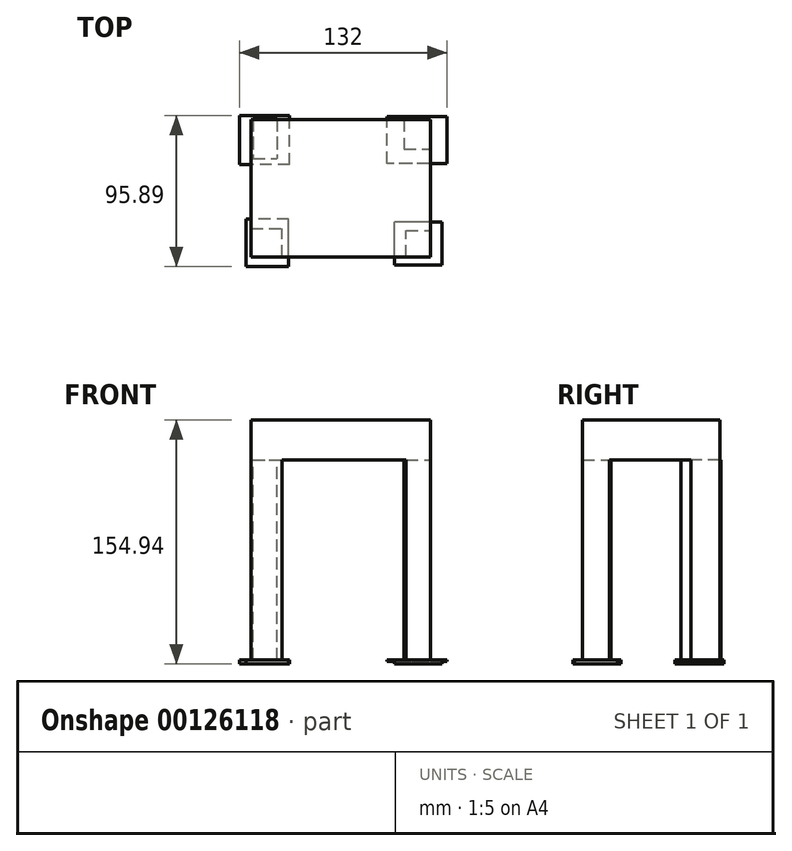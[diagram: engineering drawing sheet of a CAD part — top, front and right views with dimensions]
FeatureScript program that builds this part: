
annotation { "Feature Type Name" : "Feature", "Feature Type Description" : "" }
export const myFeature = defineFeature(function(context is Context, id is Id, definition is map)
    precondition{}
    {
        {
            var Q0;
            Q0=qCreatedBy(makeId("Top.planeOp"),FACE);
            var sketch = newSketch(context, id + "F0", { "sketchPlane" : qUnion([Q0])});
            skLineSegment(sketch, "E0.bottom", {"start": v(-57.47, 12.99) * mm, "end": v(56.4, 12.99) * mm});
            skLineSegment(sketch, "E0.top", {"start": v(-57.47, -23.38) * mm, "end": v(56.4, -23.38) * mm});
            skLineSegment(sketch, "E0.left", {"start": v(-57.47, 12.99) * mm, "end": v(-57.47, -23.38) * mm});
            skLineSegment(sketch, "E0.right", {"start": v(56.4, 12.99) * mm, "end": v(56.4, -23.38) * mm});
            skSolve(sketch);
        }
        {
            var Q0;
            Q0=makeQuery(id+"F0.imprint","IMPRINT",FACE,{"disambiguationData":[TD([[makeQuery(id+"F0.imprint","IMPRINT",EDGE,{"derivedFrom":sQuery(id+"F0.wireOp",EDGE,"E0.bottom")}),-1.0]])]});
            extrude(context, id + "F1", {"entities" : qUnion([Q0]), "depth" : 25.4 * mm});
        }
        {
            var Q0;
            Q0=makeQuery(id+"F1.opExtrude","SWEPT_FACE",FACE,{"disambiguationData":[OSD([sQuery(id+"F0.wireOp",EDGE,"E0.top")])]});
            extrude(context, id + "F2", {"entities" : qUnion([Q0]), "operationType" : NewBodyOperationType.ADD, "depth" : 50.8 * mm});
        }
        {
            var Q0;
            {var subQ0=sQuery(id+"F0.wireOp",EDGE,"E0.top");Q0=makeQuery(id+"F2.boolean.opBoolean","MERGE",FACE,{"derivedFrom":[makeQuery(id+"F1.opExtrude","CAP_FACE",FACE,{"disambiguationData":[OSD([sQuery(id+"F0.wireOp",EDGE,"E0.bottom"),subQ0,sQuery(id+"F0.wireOp",EDGE,"E0.left"),sQuery(id+"F0.wireOp",EDGE,"E0.right")])],"isStart":true}),makeQuery(id+"F2.opExtrude","SWEPT_FACE",FACE,{"disambiguationData":[OSD([subQ0]),TDD([makeQuery(id+"F1.opExtrude","CAP_EDGE",EDGE,{"disambiguationData":[OSD([subQ0])],"isStart":true})])]})]});}
            var sketch = newSketch(context, id + "F3", { "sketchPlane" : qUnion([Q0])});
            skLineSegment(sketch, "E1.bottom", {"start": v(41.09, 74.18) * mm, "end": v(56.4, 74.18) * mm});
            skLineSegment(sketch, "E1.top", {"start": v(41.09, 57.29) * mm, "end": v(56.4, 57.29) * mm});
            skLineSegment(sketch, "E1.left", {"start": v(41.09, 74.18) * mm, "end": v(41.09, 57.29) * mm});
            skLineSegment(sketch, "E1.right", {"start": v(56.4, 74.18) * mm, "end": v(56.4, 57.29) * mm});
            skSolve(sketch);
        }
        {
            var Q0;
            Q0=qSketchRegion(id+"F3",true);
            extrude(context, id + "F4", {"entities" : qUnion([Q0]), "operationType" : NewBodyOperationType.ADD, "depth" : 127 * mm});
        }
        {
            var Q0;
            {var subQ0=sQuery(id+"F0.wireOp",EDGE,"E0.top");Q0=makeQuery(id+"F2.boolean.opBoolean","MERGE",FACE,{"derivedFrom":[makeQuery(id+"F1.opExtrude","CAP_FACE",FACE,{"disambiguationData":[OSD([sQuery(id+"F0.wireOp",EDGE,"E0.bottom"),subQ0,sQuery(id+"F0.wireOp",EDGE,"E0.left"),sQuery(id+"F0.wireOp",EDGE,"E0.right")])],"isStart":true}),makeQuery(id+"F2.opExtrude","SWEPT_FACE",FACE,{"disambiguationData":[OSD([subQ0]),TDD([makeQuery(id+"F1.opExtrude","CAP_EDGE",EDGE,{"disambiguationData":[OSD([subQ0])],"isStart":true})])]})]});}
            var sketch = newSketch(context, id + "F5", { "sketchPlane" : qUnion([Q0])});
            skLineSegment(sketch, "E2.bottom", {"start": v(-57.47, 74.18) * mm, "end": v(-37.67, 74.18) * mm});
            skLineSegment(sketch, "E2.top", {"start": v(-57.47, 56.11) * mm, "end": v(-37.67, 56.11) * mm});
            skLineSegment(sketch, "E2.left", {"start": v(-57.47, 74.18) * mm, "end": v(-57.47, 56.11) * mm});
            skLineSegment(sketch, "E2.right", {"start": v(-37.67, 74.18) * mm, "end": v(-37.67, 56.11) * mm});
            skSolve(sketch);
        }
        {
            var Q0;
            Q0=qSketchRegion(id+"F5",true);
            extrude(context, id + "F6", {"entities" : qUnion([Q0]), "operationType" : NewBodyOperationType.ADD, "depth" : 127 * mm});
        }
        {
            var Q0;
            {var subQ0=sQuery(id+"F0.wireOp",EDGE,"E0.top");Q0=makeQuery(id+"F2.boolean.opBoolean","MERGE",FACE,{"derivedFrom":[makeQuery(id+"F1.opExtrude","CAP_FACE",FACE,{"disambiguationData":[OSD([sQuery(id+"F0.wireOp",EDGE,"E0.bottom"),subQ0,sQuery(id+"F0.wireOp",EDGE,"E0.left"),sQuery(id+"F0.wireOp",EDGE,"E0.right")])],"isStart":true}),makeQuery(id+"F2.opExtrude","SWEPT_FACE",FACE,{"disambiguationData":[OSD([subQ0]),TDD([makeQuery(id+"F1.opExtrude","CAP_EDGE",EDGE,{"disambiguationData":[OSD([subQ0])],"isStart":true})])]})]});}
            var sketch = newSketch(context, id + "F7", { "sketchPlane" : qUnion([Q0])});
            skLineSegment(sketch, "E3.bottom", {"start": v(39.63, -12.99) * mm, "end": v(56.4, -12.99) * mm});
            skLineSegment(sketch, "E3.top", {"start": v(39.63, 5.6) * mm, "end": v(56.4, 5.6) * mm});
            skLineSegment(sketch, "E3.left", {"start": v(39.63, -12.99) * mm, "end": v(39.63, 5.6) * mm});
            skLineSegment(sketch, "E3.right", {"start": v(56.4, -12.99) * mm, "end": v(56.4, 5.6) * mm});
            skSolve(sketch);
        }
        {
            var Q0;
            {var subQ4=sQuery(id+"F7.wireOp",EDGE,"E3.top");Q0=makeQuery(id+"F7.imprint","IMPRINT",FACE,{"disambiguationData":[TD([[makeQuery(id+"F7.imprint","IMPRINT",EDGE,{"derivedFrom":subQ4}),1.0]])]});}
            var sketch = newSketch(context, id + "F8", { "sketchPlane" : qUnion([Q0])});
            skSolve(sketch);
        }
        {
            var Q0;
            Q0=makeQuery(id+"F7.imprint","IMPRINT",FACE,{"disambiguationData":[TD([[makeQuery(id+"F7.imprint","IMPRINT",EDGE,{"derivedFrom":sQuery(id+"F7.wireOp",EDGE,"E3.bottom")}),1.0]])]});
            extrude(context, id + "F9", {"entities" : qUnion([Q0]), "operationType" : NewBodyOperationType.ADD, "depth" : 127 * mm});
        }
        {
            var Q0;
            {var subQ4=sQuery(id+"F7.wireOp",EDGE,"E3.top");Q0=makeQuery(id+"F8.imprint","IMPRINT",FACE,{"disambiguationData":[TD([[makeQuery(id+"F8.imprint","IMPRINT",EDGE,{"derivedFrom":makeQuery(id+"F7.imprint","IMPRINT",EDGE,{"derivedFrom":subQ4})}),1.0]])]});}
            var sketch = newSketch(context, id + "F10", { "sketchPlane" : qUnion([Q0])});
            skLineSegment(sketch, "E4.bottom", {"start": v(-56.19, -13.73) * mm, "end": v(-41.1, -13.73) * mm});
            skLineSegment(sketch, "E4.top", {"start": v(-56.19, 11.67) * mm, "end": v(-41.1, 11.67) * mm});
            skLineSegment(sketch, "E4.left", {"start": v(-56.19, -13.73) * mm, "end": v(-56.19, 11.67) * mm});
            skLineSegment(sketch, "E4.right", {"start": v(-41.1, -13.73) * mm, "end": v(-41.1, 11.67) * mm});
            skSolve(sketch);
        }
        {
            var Q0;
            Q0=qSketchRegion(id+"F10",true);
            extrude(context, id + "F11", {"entities" : qUnion([Q0]), "operationType" : NewBodyOperationType.ADD, "depth" : 25.4 * mm});
        }
        {
            var Q0;
            Q0=makeQuery(id+"F11.opExtrude","CAP_FACE",FACE,{"disambiguationData":[OSD([sQuery(id+"F10.wireOp",EDGE,"E4.bottom"),sQuery(id+"F10.wireOp",EDGE,"E4.top"),sQuery(id+"F10.wireOp",EDGE,"E4.left"),sQuery(id+"F10.wireOp",EDGE,"E4.right")])],"isStart":false});
            var sketch = newSketch(context, id + "F12", { "sketchPlane" : qUnion([Q0])});
            skSolve(sketch);
        }
        {
            var Q0;
            Q0=makeQuery(id+"F12.imprint","IMPRINT",FACE,{"disambiguationData":[TD([[makeQuery(id+"F12.imprint","IMPRINT",EDGE,{"derivedFrom":makeQuery(id+"F11.opExtrude","CAP_EDGE",EDGE,{"disambiguationData":[OSD([sQuery(id+"F10.wireOp",EDGE,"E4.bottom")])],"isStart":false})}),1.0]])]});
            extrude(context, id + "F13", {"entities" : qUnion([Q0]), "operationType" : NewBodyOperationType.ADD, "depth" : 101.6 * mm});
        }
        {
            var Q0;
            Q0=makeQuery(id+"F13.opExtrude","CAP_FACE",FACE,{"disambiguationData":[OSD([sQuery(id+"F10.wireOp",EDGE,"E4.bottom"),sQuery(id+"F10.wireOp",EDGE,"E4.top"),sQuery(id+"F10.wireOp",EDGE,"E4.left"),sQuery(id+"F10.wireOp",EDGE,"E4.right")])],"isStart":false});
            var sketch = newSketch(context, id + "F14", { "sketchPlane" : qUnion([Q0])});
            skLineSegment(sketch, "E5.bottom", {"start": v(-32.93, 15.63) * mm, "end": v(-64.92, 15.63) * mm});
            skLineSegment(sketch, "E5.top", {"start": v(-32.93, -15.63) * mm, "end": v(-64.92, -15.63) * mm});
            skLineSegment(sketch, "E5.left", {"start": v(-32.93, 15.63) * mm, "end": v(-32.93, -15.63) * mm});
            skLineSegment(sketch, "E5.right", {"start": v(-64.92, 15.63) * mm, "end": v(-64.92, -15.63) * mm});
            skPoint(sketch, "E5.middle", {"position": v(-48.92, 0) * mm});
            skSolve(sketch);
        }
        {
            var Q0;
            Q0=qSketchRegion(id+"F14",true);
            extrude(context, id + "F15", {"entities" : qUnion([Q0]), "operationType" : NewBodyOperationType.ADD, "depth" : 2.54 * mm});
        }
        {
            var Q0;
            Q0=makeQuery(id+"F6.opExtrude","CAP_FACE",FACE,{"disambiguationData":[OSD([sQuery(id+"F5.wireOp",EDGE,"E2.bottom"),sQuery(id+"F5.wireOp",EDGE,"E2.top"),sQuery(id+"F5.wireOp",EDGE,"E2.left"),sQuery(id+"F5.wireOp",EDGE,"E2.right")])],"isStart":false});
            var sketch = newSketch(context, id + "F16", { "sketchPlane" : qUnion([Q0])});
            skLineSegment(sketch, "E6.bottom", {"start": v(-33.59, 80.26) * mm, "end": v(-60.7, 80.26) * mm});
            skLineSegment(sketch, "E6.top", {"start": v(-33.59, 50.03) * mm, "end": v(-60.7, 50.03) * mm});
            skLineSegment(sketch, "E6.left", {"start": v(-33.59, 80.26) * mm, "end": v(-33.59, 50.03) * mm});
            skLineSegment(sketch, "E6.right", {"start": v(-60.7, 80.26) * mm, "end": v(-60.7, 50.03) * mm});
            skPoint(sketch, "E6.middle", {"position": v(-47.14, 65.14) * mm});
            skPoint(sketch, "E6.middle.positionSnap0", {"position": v(-37.67, 65.14) * mm});
            skPoint(sketch, "E6.centerSnap0", {"position": v(-37.67, 65.14) * mm});
            skSolve(sketch);
        }
        {
            var Q0;
            Q0=qSketchRegion(id+"F16",true);
            extrude(context, id + "F17", {"entities" : qUnion([Q0]), "operationType" : NewBodyOperationType.ADD, "depth" : 2.54 * mm});
        }
        {
            var Q0;
            Q0=makeQuery(id+"F9.opExtrude","CAP_FACE",FACE,{"disambiguationData":[OSD([sQuery(id+"F7.wireOp",EDGE,"E3.bottom"),sQuery(id+"F7.wireOp",EDGE,"E3.top"),sQuery(id+"F7.wireOp",EDGE,"E3.left"),sQuery(id+"F7.wireOp",EDGE,"E3.right")])],"isStart":false});
            var sketch = newSketch(context, id + "F18", { "sketchPlane" : qUnion([Q0])});
            skLineSegment(sketch, "E7.bottom", {"start": v(67.08, 14.85) * mm, "end": v(28.96, 14.85) * mm});
            skLineSegment(sketch, "E7.top", {"start": v(67.08, -14.85) * mm, "end": v(28.96, -14.85) * mm});
            skLineSegment(sketch, "E7.left", {"start": v(67.08, 14.85) * mm, "end": v(67.08, -14.85) * mm});
            skLineSegment(sketch, "E7.right", {"start": v(28.96, 14.85) * mm, "end": v(28.96, -14.85) * mm});
            skPoint(sketch, "E7.middle", {"position": v(48.02, 0) * mm});
            skPoint(sketch, "E7.middle.positionSnap0", {"position": v(48.02, -12.99) * mm});
            skPoint(sketch, "E7.centerSnap0", {"position": v(48.02, -12.99) * mm});
            skSolve(sketch);
        }
        {
            var Q0;
            Q0=qSketchRegion(id+"F18",true);
            extrude(context, id + "F19", {"entities" : qUnion([Q0]), "operationType" : NewBodyOperationType.ADD, "depth" : 1 * mm});
        }
        {
            var Q0;
            Q0=makeQuery(id+"F4.opExtrude","CAP_FACE",FACE,{"disambiguationData":[OSD([sQuery(id+"F3.wireOp",EDGE,"E1.bottom"),sQuery(id+"F3.wireOp",EDGE,"E1.top"),sQuery(id+"F3.wireOp",EDGE,"E1.left"),sQuery(id+"F3.wireOp",EDGE,"E1.right")])],"isStart":false});
            var sketch = newSketch(context, id + "F20", { "sketchPlane" : qUnion([Q0])});
            skLineSegment(sketch, "E8.bottom", {"start": v(63.88, 79.36) * mm, "end": v(33.58, 79.36) * mm});
            skLineSegment(sketch, "E8.top", {"start": v(63.88, 52.1) * mm, "end": v(33.58, 52.1) * mm});
            skLineSegment(sketch, "E8.left", {"start": v(63.88, 79.36) * mm, "end": v(63.88, 52.1) * mm});
            skLineSegment(sketch, "E8.right", {"start": v(33.58, 79.36) * mm, "end": v(33.58, 52.1) * mm});
            skPoint(sketch, "E8.middle", {"position": v(48.73, 65.73) * mm});
            skPoint(sketch, "E8.middle.positionSnap0", {"position": v(56.4, 65.73) * mm});
            skPoint(sketch, "E8.centerSnap0", {"position": v(56.4, 65.73) * mm});
            skSolve(sketch);
        }
        {
            var Q0;
            Q0=qSketchRegion(id+"F20",true);
            extrude(context, id + "F21", {"entities" : qUnion([Q0]), "operationType" : NewBodyOperationType.ADD, "depth" : 2.54 * mm});
        }
    });
